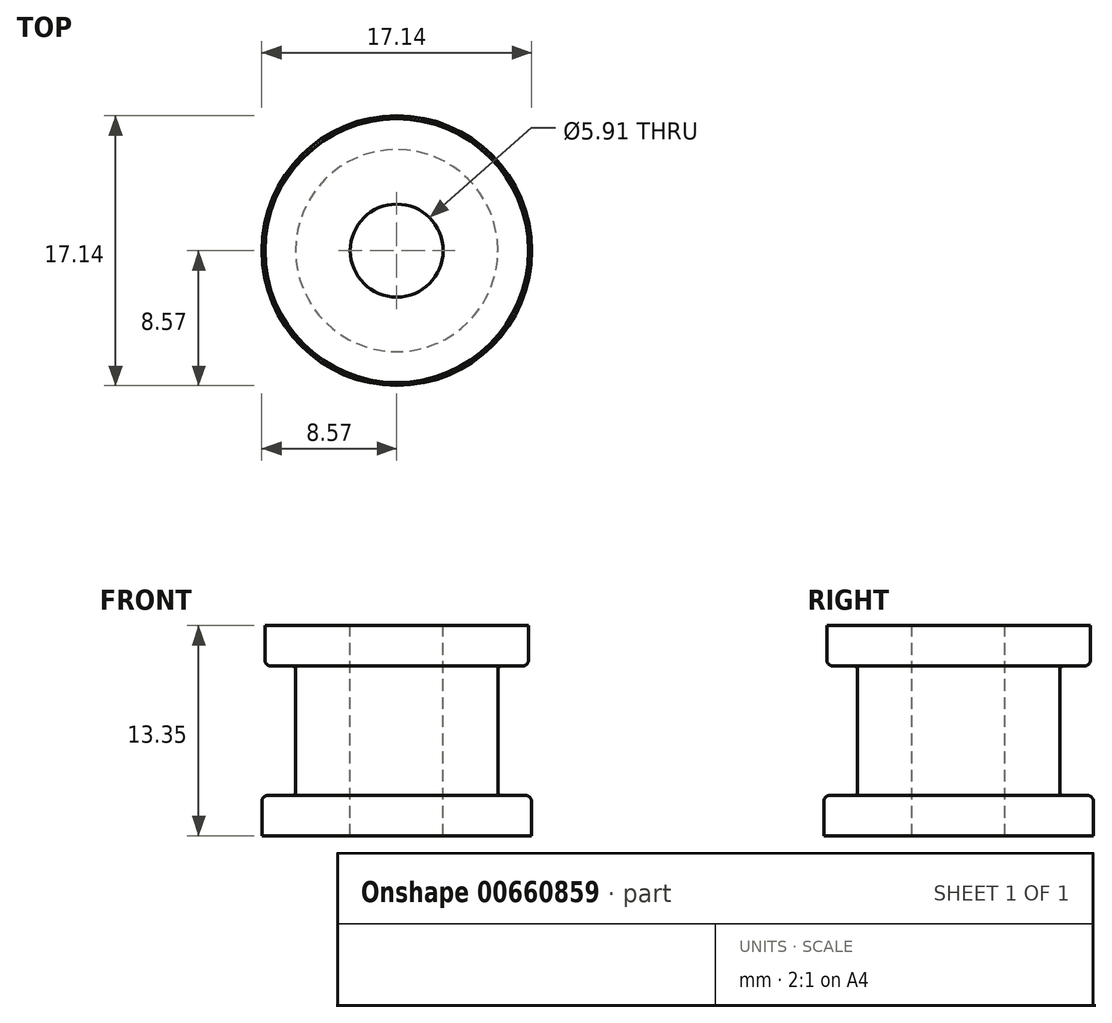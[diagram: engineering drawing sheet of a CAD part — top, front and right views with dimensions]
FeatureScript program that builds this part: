
annotation { "Feature Type Name" : "Feature", "Feature Type Description" : "" }
export const myFeature = defineFeature(function(context is Context, id is Id, definition is map)
    precondition{}
    {
        {
            var Q0;
            Q0=qCreatedBy(makeId("Right.planeOp"),FACE);
            var sketch = newSketch(context, id + "F0", { "sketchPlane" : qUnion([Q0])});
            skLineSegment(sketch, "E0", {"start": v(0, 0) * mm, "end": v(-2.95, 0) * mm});
            skLineSegment(sketch, "E1", {"start": v(-2.95, 0) * mm, "end": v(-8.38, 0) * mm});
            skLineSegment(sketch, "E2", {"start": v(0, 0) * mm, "end": v(0, -13.35) * mm});
            skLineSegment(sketch, "E3", {"start": v(-2.95, 0) * mm, "end": v(-2.95, -6.67) * mm});
            skLineSegment(sketch, "E4", {"start": v(-2.95, -6.67) * mm, "end": v(-2.95, -13.35) * mm});
            skLineSegment(sketch, "E5", {"start": v(-8.38, 0) * mm, "end": v(-8.38, -2.17) * mm});
            skLineSegment(sketch, "E6.0", {"start": v(-2.95, -13.35) * mm, "end": v(-8.57, -13.35) * mm});
            skLineSegment(sketch, "E7", {"start": v(-8.57, -13.35) * mm, "end": v(-8.57, -11.18) * mm});
            skLineSegment(sketch, "E8", {"start": v(-7.97, -2.57) * mm, "end": v(-6.64, -2.57) * mm});
            skLineSegment(sketch, "E9", {"start": v(-8.16, -10.78) * mm, "end": v(-6.64, -10.78) * mm});
            skLineSegment(sketch, "E10", {"start": v(-6.42, -2.79) * mm, "end": v(-6.42, -10.56) * mm});
            skPoint(sketch, "E11.visualSharp", {"position": v(-8.38, -2.57) * mm});
            skArc(sketch, "E11.filletArc", {"start": v(-8.38, -2.17) * mm, "mid": v(-8.26, -2.45) * mm, "end": v(-7.97, -2.57) * mm});
            skPoint(sketch, "E12.visualSharp", {"position": v(-6.42, -2.57) * mm});
            skArc(sketch, "E12.filletArc", {"start": v(-6.42, -2.79) * mm, "mid": v(-6.48, -2.63) * mm, "end": v(-6.64, -2.57) * mm});
            skPoint(sketch, "E13.visualSharp", {"position": v(-6.42, -10.78) * mm});
            skArc(sketch, "E13.filletArc", {"start": v(-6.64, -10.78) * mm, "mid": v(-6.48, -10.71) * mm, "end": v(-6.42, -10.56) * mm});
            skPoint(sketch, "E14.visualSharp", {"position": v(-8.57, -10.78) * mm});
            skArc(sketch, "E14.filletArc", {"start": v(-8.16, -10.78) * mm, "mid": v(-8.45, -10.9) * mm, "end": v(-8.57, -11.18) * mm});
            skSolve(sketch);
        }
        {
            var Q0;
            Q0=makeQuery(id+"F0.imprint","IMPRINT",FACE,{"disambiguationData":[TD([[makeQuery(id+"F0.imprint","IMPRINT",EDGE,{"derivedFrom":sQuery(id+"F0.wireOp",EDGE,"E1")}),1.0]])]});
            var Q1;
            Q1=sQuery(id+"F0.wireOp",EDGE,"E2");
            revolve(context, id + "F1", {"entities" : qUnion([Q0]), "axis" : qUnion([Q1]), "revolveType" : RevolveType.FULL});
        }
    });
